# Revit family: Hekatron_Feststellanlagen_Drucktaster 422 Ex_DE_22.01
name_source: partatom
category: Brandmelder
revit_build: Autodesk Revit 2018 (Build: 20190510_1515(x64)
units: mm (PartAtom-declared; Revit-internal decimal feet)

## family parameters
Basisbauteil = Fläche
Beim Laden mit Abzugskörper schneiden = Nein
Bemaßung runder Anschluss = Durchmesser verwenden
Beschriftungsausrichtung beibehalten = Ja
Gemeinsam genutzt = Nein
OmniClass-Nummer = 23.85.30.21
OmniClass-Titel = Environmental Detection/Registration
Raumberechnungspunkt = Nein
Teiletyp = Normal

## types (1)
- Push button 422 Ex
    Beschreibung = Handauslösetaster zur Montage in den Ex-Zonen 1, 2 und 22, zum manuellen Auslösen von Feststellvorrichtungen gemäß den DIBt-Richtlinien und ATEX.
    Betriebsspannung = 24 V DC
    Breite (mm) = 91.0
    Ex-Zonen = 1, 2, 21, 22
    Farbe = scharz, rot
    Hersteller = Hekatron
    Höhe (mm) = 91.0
    Kabeleinführung = oben, unten
    Link zu Ausschreibungstext = https://www.meinhplus.de
    Link zu Produktinformation = https://www.hekatron-planungstools.de
    Link zu ausschreiben.de = http://www.ausschreiben.de
    Material = Thermoplast
    Modell = Drucktaster 422 Ex
    Montageart = Aufputz
    Schutzart = IP 65
    Tiefe (mm) = 88.0
    Typenkommentare = Drucktaster 422 Ex
    UB A&S Artikel Nummer = 6500141
    URL = https://www.hekatron-brandschutz.de
    Version des BIM Objektes = 22.01
    Vorgabe-Ansicht = 1200 mm
    Zulässige Umgebungstemperatur = -50 °C bis +60 °C

## geometry (parser evidence)
native form markers: Sweep x2
no freeform markers — native parametric forms only
